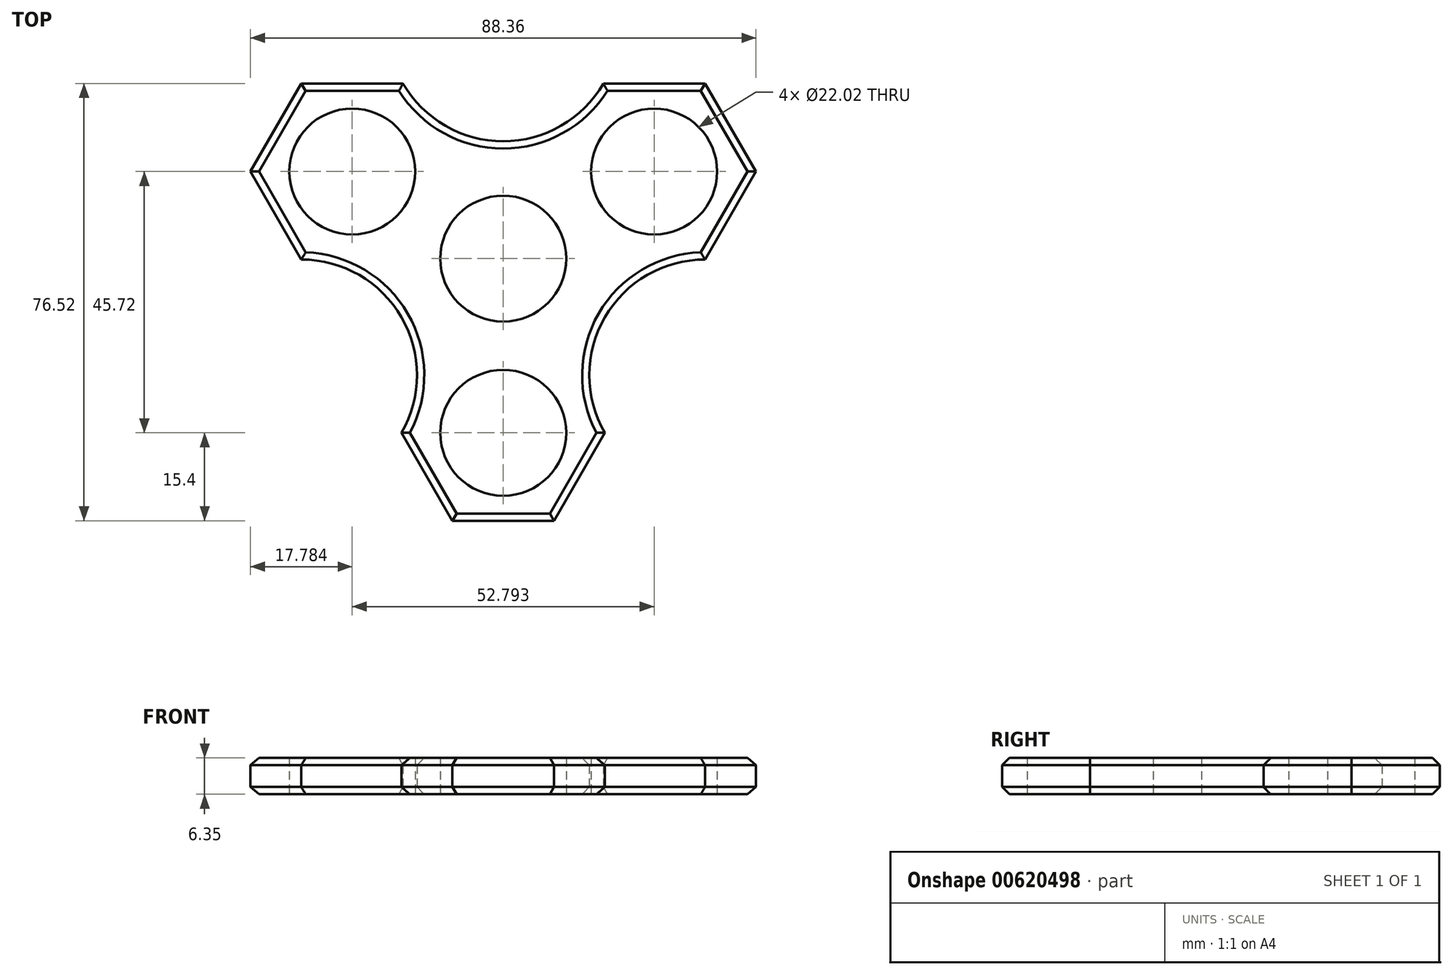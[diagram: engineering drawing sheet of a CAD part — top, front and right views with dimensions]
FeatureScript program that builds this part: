
annotation { "Feature Type Name" : "Feature", "Feature Type Description" : "" }
export const myFeature = defineFeature(function(context is Context, id is Id, definition is map)
    precondition{}
    {
        {
            var Q0;
            Q0=qCreatedBy(makeId("Top.planeOp"),FACE);
            var sketch = newSketch(context, id + "F0", { "sketchPlane" : qUnion([Q0])});
            skCircle(sketch, "E0", {"center": v(0, 0) * mm, "radius": 11.01 * mm});
            skLineSegment(sketch, "E1", {"start": v(0, 0) * mm, "end": v(-26.4, 15.24) * mm});
            skLineSegment(sketch, "E2", {"start": v(0, 0) * mm, "end": v(26.4, 15.24) * mm});
            skLineSegment(sketch, "E3", {"start": v(0, 0) * mm, "end": v(0, -30.48) * mm});
            skCircle(sketch, "E4", {"center": v(26.4, 15.24) * mm, "radius": 11.01 * mm});
            skCircle(sketch, "E5", {"center": v(-26.4, 15.24) * mm, "radius": 11.01 * mm});
            skCircle(sketch, "E6", {"center": v(0, -30.48) * mm, "radius": 11.01 * mm});
            skCircle(sketch, "E7.cCircle", {"center": v(-26.4, 15.24) * mm, "radius": 17.78 * mm, "construction": true});
            skLineSegment(sketch, "E7.0", {"start": v(-35.29, -0.16) * mm, "end": v(-44.18, 15.24) * mm});
            skLineSegment(sketch, "E7.1", {"start": v(-44.18, 15.24) * mm, "end": v(-35.29, 30.64) * mm});
            skLineSegment(sketch, "E7.2", {"start": v(-35.29, 30.64) * mm, "end": v(-17.5, 30.64) * mm});
            skLineSegment(sketch, "E7.3", {"start": v(-17.5, 30.64) * mm, "end": v(-8.62, 15.24) * mm});
            skLineSegment(sketch, "E7.4", {"start": v(-8.62, 15.24) * mm, "end": v(-17.5, -0.16) * mm});
            skLineSegment(sketch, "E7.5", {"start": v(-17.5, -0.16) * mm, "end": v(-35.29, -0.16) * mm});
            skCircle(sketch, "E8.cCircle", {"center": v(26.4, 15.24) * mm, "radius": 17.78 * mm, "construction": true});
            skLineSegment(sketch, "E8.0", {"start": v(35.29, -0.16) * mm, "end": v(17.5, -0.16) * mm});
            skLineSegment(sketch, "E8.1", {"start": v(17.5, -0.16) * mm, "end": v(8.62, 15.24) * mm});
            skLineSegment(sketch, "E8.2", {"start": v(8.62, 15.24) * mm, "end": v(17.5, 30.64) * mm});
            skLineSegment(sketch, "E8.3", {"start": v(17.5, 30.64) * mm, "end": v(35.29, 30.64) * mm});
            skLineSegment(sketch, "E8.4", {"start": v(35.29, 30.64) * mm, "end": v(44.18, 15.24) * mm});
            skLineSegment(sketch, "E8.5", {"start": v(44.18, 15.24) * mm, "end": v(35.29, -0.16) * mm});
            skCircle(sketch, "E9.cCircle", {"center": v(0, -30.48) * mm, "radius": 17.78 * mm, "construction": true});
            skLineSegment(sketch, "E9.0", {"start": v(-8.9, -45.88) * mm, "end": v(-17.78, -30.48) * mm});
            skLineSegment(sketch, "E9.1", {"start": v(-17.78, -30.48) * mm, "end": v(-8.89, -15.08) * mm});
            skLineSegment(sketch, "E9.2", {"start": v(-8.9, -15.08) * mm, "end": v(8.9, -15.08) * mm});
            skLineSegment(sketch, "E9.3", {"start": v(8.9, -15.08) * mm, "end": v(17.78, -30.48) * mm});
            skLineSegment(sketch, "E9.4", {"start": v(17.78, -30.48) * mm, "end": v(8.9, -45.88) * mm});
            skLineSegment(sketch, "E9.5", {"start": v(8.89, -45.88) * mm, "end": v(-8.9, -45.88) * mm});
            skArc(sketch, "E10", {"start": v(-17.78, -30.48) * mm, "mid": v(-17.78, -10.27) * mm, "end": v(-35.29, -0.16) * mm});
            skArc(sketch, "E11", {"start": v(35.29, -0.16) * mm, "mid": v(17.78, -10.27) * mm, "end": v(17.78, -30.48) * mm});
            skArc(sketch, "E12", {"start": v(-17.5, 30.64) * mm, "mid": v(0, 20.53) * mm, "end": v(17.5, 30.64) * mm});
            skSolve(sketch);
        }
        {
            var Q0;
            Q0 = qSketchRegion(id + "F0", true);
            extrude(context, id + "F1", {"entities" : qUnion([Q0]), "depth" : 6.35 * mm, "offsetDistance" : 25.4 * mm});
        }
        {
            var Q0;
            Q0=makeQuery(id+"F1.opExtrude","CAP_EDGE",EDGE,{"disambiguationData":[OSD([sQuery(id+"F0.wireOp",EDGE,"E7.2")])],"isStart":false});
            var Q1;
            Q1=makeQuery(id+"F1.opExtrude","CAP_EDGE",EDGE,{"disambiguationData":[OSD([sQuery(id+"F0.wireOp",EDGE,"E12")])],"isStart":false});
            var Q2;
            Q2=makeQuery(id+"F1.opExtrude","CAP_EDGE",EDGE,{"disambiguationData":[OSD([sQuery(id+"F0.wireOp",EDGE,"E8.3")])],"isStart":false});
            var Q3;
            Q3=makeQuery(id+"F1.opExtrude","CAP_EDGE",EDGE,{"disambiguationData":[OSD([sQuery(id+"F0.wireOp",EDGE,"E8.4")])],"isStart":false});
            var Q4;
            Q4=makeQuery(id+"F1.opExtrude","CAP_EDGE",EDGE,{"disambiguationData":[OSD([sQuery(id+"F0.wireOp",EDGE,"E8.5")])],"isStart":false});
            var Q5;
            Q5=makeQuery(id+"F1.opExtrude","CAP_EDGE",EDGE,{"disambiguationData":[OSD([sQuery(id+"F0.wireOp",EDGE,"E11")])],"isStart":false});
            var Q6;
            Q6=makeQuery(id+"F1.opExtrude","CAP_EDGE",EDGE,{"disambiguationData":[OSD([sQuery(id+"F0.wireOp",EDGE,"E9.4")])],"isStart":false});
            var Q7;
            Q7=makeQuery(id+"F1.opExtrude","CAP_EDGE",EDGE,{"disambiguationData":[OSD([sQuery(id+"F0.wireOp",EDGE,"E9.5")])],"isStart":false});
            var Q8;
            Q8=makeQuery(id+"F1.opExtrude","CAP_EDGE",EDGE,{"disambiguationData":[OSD([sQuery(id+"F0.wireOp",EDGE,"E9.0")])],"isStart":false});
            var Q9;
            Q9=makeQuery(id+"F1.opExtrude","CAP_EDGE",EDGE,{"disambiguationData":[OSD([sQuery(id+"F0.wireOp",EDGE,"E10")])],"isStart":false});
            var Q10;
            Q10=makeQuery(id+"F1.opExtrude","CAP_EDGE",EDGE,{"disambiguationData":[OSD([sQuery(id+"F0.wireOp",EDGE,"E7.0")])],"isStart":false});
            var Q11;
            Q11=makeQuery(id+"F1.opExtrude","CAP_EDGE",EDGE,{"disambiguationData":[OSD([sQuery(id+"F0.wireOp",EDGE,"E7.1")])],"isStart":false});
            chamfer(context, id + "F2", {"entities" : qUnion([Q0, Q1, Q2, Q3, Q4, Q5, Q6, Q7, Q8, Q9, Q10, Q11]), "width" : 1.27 * mm, "tangentPropagation" : true});
        }
        {
            var Q0;
            Q0=makeQuery(id+"F1.opExtrude","CAP_EDGE",EDGE,{"disambiguationData":[OSD([sQuery(id+"F0.wireOp",EDGE,"E9.5")])],"isStart":true});
            var Q1;
            Q1=makeQuery(id+"F1.opExtrude","CAP_EDGE",EDGE,{"disambiguationData":[OSD([sQuery(id+"F0.wireOp",EDGE,"E9.4")])],"isStart":true});
            var Q2;
            Q2=makeQuery(id+"F1.opExtrude","CAP_EDGE",EDGE,{"disambiguationData":[OSD([sQuery(id+"F0.wireOp",EDGE,"E11")])],"isStart":true});
            var Q3;
            Q3=makeQuery(id+"F1.opExtrude","CAP_EDGE",EDGE,{"disambiguationData":[OSD([sQuery(id+"F0.wireOp",EDGE,"E8.5")])],"isStart":true});
            var Q4;
            Q4=makeQuery(id+"F1.opExtrude","CAP_EDGE",EDGE,{"disambiguationData":[OSD([sQuery(id+"F0.wireOp",EDGE,"E8.4")])],"isStart":true});
            var Q5;
            Q5=makeQuery(id+"F1.opExtrude","CAP_EDGE",EDGE,{"disambiguationData":[OSD([sQuery(id+"F0.wireOp",EDGE,"E8.3")])],"isStart":true});
            var Q6;
            Q6=makeQuery(id+"F1.opExtrude","CAP_EDGE",EDGE,{"disambiguationData":[OSD([sQuery(id+"F0.wireOp",EDGE,"E12")])],"isStart":true});
            var Q7;
            Q7=makeQuery(id+"F1.opExtrude","CAP_EDGE",EDGE,{"disambiguationData":[OSD([sQuery(id+"F0.wireOp",EDGE,"E7.2")])],"isStart":true});
            var Q8;
            Q8=makeQuery(id+"F1.opExtrude","CAP_EDGE",EDGE,{"disambiguationData":[OSD([sQuery(id+"F0.wireOp",EDGE,"E7.1")])],"isStart":true});
            var Q9;
            Q9=makeQuery(id+"F1.opExtrude","CAP_EDGE",EDGE,{"disambiguationData":[OSD([sQuery(id+"F0.wireOp",EDGE,"E7.0")])],"isStart":true});
            var Q10;
            Q10=makeQuery(id+"F1.opExtrude","CAP_EDGE",EDGE,{"disambiguationData":[OSD([sQuery(id+"F0.wireOp",EDGE,"E10")])],"isStart":true});
            var Q11;
            Q11=makeQuery(id+"F1.opExtrude","CAP_EDGE",EDGE,{"disambiguationData":[OSD([sQuery(id+"F0.wireOp",EDGE,"E9.0")])],"isStart":true});
            chamfer(context, id + "F3", {"entities" : qUnion([Q0, Q1, Q2, Q3, Q4, Q5, Q6, Q7, Q8, Q9, Q10, Q11]), "width" : 1.27 * mm, "tangentPropagation" : true});
        }
    });
